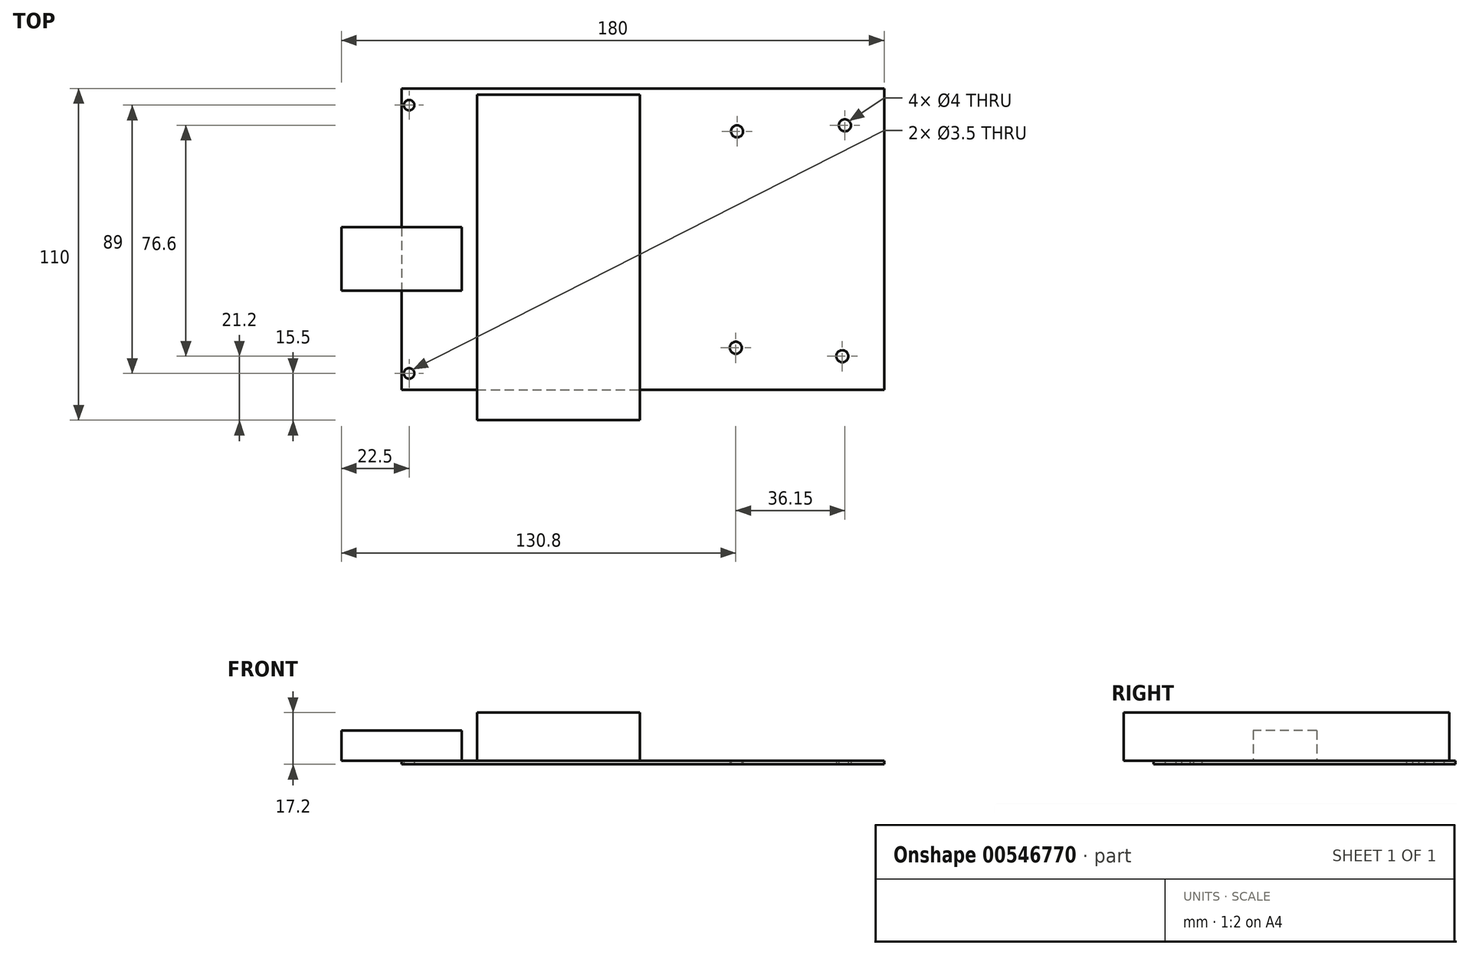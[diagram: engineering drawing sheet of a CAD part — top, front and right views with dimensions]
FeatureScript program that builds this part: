
annotation { "Feature Type Name" : "Feature", "Feature Type Description" : "" }
export const myFeature = defineFeature(function(context is Context, id is Id, definition is map)
    precondition{}
    {
        {
            var Q0;
            Q0=qCreatedBy(makeId("Front.planeOp"),FACE);
            var sketch = newSketch(context, id + "F0", { "sketchPlane" : qUnion([Q0])});
            skSolve(sketch);
        }
        {
            var Q0;
            Q0=qCreatedBy(makeId("Top.planeOp"),FACE);
            var sketch = newSketch(context, id + "F1", { "sketchPlane" : qUnion([Q0])});
            skLineSegment(sketch, "E0.bottom", {"start": v(-80, 50) * mm, "end": v(80, 50) * mm});
            skLineSegment(sketch, "E0.top", {"start": v(-80, -50) * mm, "end": v(80, -50) * mm});
            skLineSegment(sketch, "E0.left", {"start": v(-80, 50) * mm, "end": v(-80, -50) * mm});
            skLineSegment(sketch, "E0.right", {"start": v(80, 50) * mm, "end": v(80, -50) * mm});
            skPoint(sketch, "E0.middle", {"position": v(0, 0) * mm});
            skCircle(sketch, "E1", {"center": v(-77.5, 44.5) * mm, "radius": 1.75 * mm});
            skCircle(sketch, "E2.MirrorC", {"center": v(-77.5, -44.5) * mm, "radius": 1.75 * mm});
            skCircle(sketch, "E3", {"center": v(66.95, 37.8) * mm, "radius": 2 * mm});
            skCircle(sketch, "E4", {"center": v(66.1, -38.8) * mm, "radius": 2 * mm});
            skCircle(sketch, "E5", {"center": v(31.2, 35.8) * mm, "radius": 2 * mm});
            skCircle(sketch, "E6", {"center": v(30.8, -36) * mm, "radius": 2 * mm});
            skSolve(sketch);
        }
        {
            var Q0;
            Q0 = qSketchRegion(id + "F0", true);
            var Q1;
            Q1 = qSketchRegion(id + "F1", true);
            extrude(context, id + "F2", {"entities" : qUnion([Q0, Q1]), "depth" : 1.2 * mm, "offsetDistance" : 25 * mm, "symmetric" : true});
        }
        {
            var Q0;
            Q0=makeQuery(id+"F2.opExtrude","CAP_FACE",FACE,{"disambiguationData":[OSD([sQuery(id+"F1.wireOp",EDGE,"E0.bottom"),sQuery(id+"F1.wireOp",EDGE,"E0.top"),sQuery(id+"F1.wireOp",EDGE,"E0.left"),sQuery(id+"F1.wireOp",EDGE,"E0.right"),sQuery(id+"F1.wireOp",EDGE,"E1"),sQuery(id+"F1.wireOp",EDGE,"E2.MirrorC"),sQuery(id+"F1.wireOp",EDGE,"E3"),sQuery(id+"F1.wireOp",EDGE,"E4"),sQuery(id+"F1.wireOp",EDGE,"E5"),sQuery(id+"F1.wireOp",EDGE,"E6")])],"isStart":false});
            var sketch = newSketch(context, id + "F3", { "sketchPlane" : qUnion([Q0])});
            skLineSegment(sketch, "E7.bottom", {"start": v(-1, -60) * mm, "end": v(-55, -60) * mm});
            skLineSegment(sketch, "E7.top", {"start": v(-1, 48) * mm, "end": v(-55, 48) * mm});
            skLineSegment(sketch, "E7.left", {"start": v(-1, -60) * mm, "end": v(-1, 48) * mm});
            skLineSegment(sketch, "E7.right", {"start": v(-55, -60) * mm, "end": v(-55, 48) * mm});
            skPoint(sketch, "E7.middle", {"position": v(-28, -6) * mm});
            skSolve(sketch);
        }
        {
            var Q0;
            Q0 = qSketchRegion(id + "F3", true);
            extrude(context, id + "F4", {"entities" : qUnion([Q0]), "operationType" : NewBodyOperationType.ADD, "depth" : 16 * mm, "offsetDistance" : 25 * mm});
        }
        {
            var Q0;
            Q0=makeQuery(id+"F2.opExtrude","CAP_FACE",FACE,{"disambiguationData":[OSD([sQuery(id+"F1.wireOp",EDGE,"E0.bottom"),sQuery(id+"F1.wireOp",EDGE,"E0.top"),sQuery(id+"F1.wireOp",EDGE,"E0.left"),sQuery(id+"F1.wireOp",EDGE,"E0.right"),sQuery(id+"F1.wireOp",EDGE,"E1"),sQuery(id+"F1.wireOp",EDGE,"E2.MirrorC"),sQuery(id+"F1.wireOp",EDGE,"E3"),sQuery(id+"F1.wireOp",EDGE,"E4"),sQuery(id+"F1.wireOp",EDGE,"E5"),sQuery(id+"F1.wireOp",EDGE,"E6")])],"isStart":false});
            var sketch = newSketch(context, id + "F5", { "sketchPlane" : qUnion([Q0])});
            skLineSegment(sketch, "E8.bottom", {"start": v(-60, 4) * mm, "end": v(-100, 4) * mm});
            skLineSegment(sketch, "E8.top", {"start": v(-60, -17) * mm, "end": v(-100, -17) * mm});
            skLineSegment(sketch, "E8.left", {"start": v(-60, 4) * mm, "end": v(-60, -17) * mm});
            skLineSegment(sketch, "E8.right", {"start": v(-100, 4) * mm, "end": v(-100, -17) * mm});
            skSolve(sketch);
        }
        {
            var Q0;
            Q0 = qSketchRegion(id + "F5", true);
            extrude(context, id + "F6", {"entities" : qUnion([Q0]), "operationType" : NewBodyOperationType.ADD, "depth" : 10 * mm, "offsetDistance" : 25 * mm});
        }
    });
